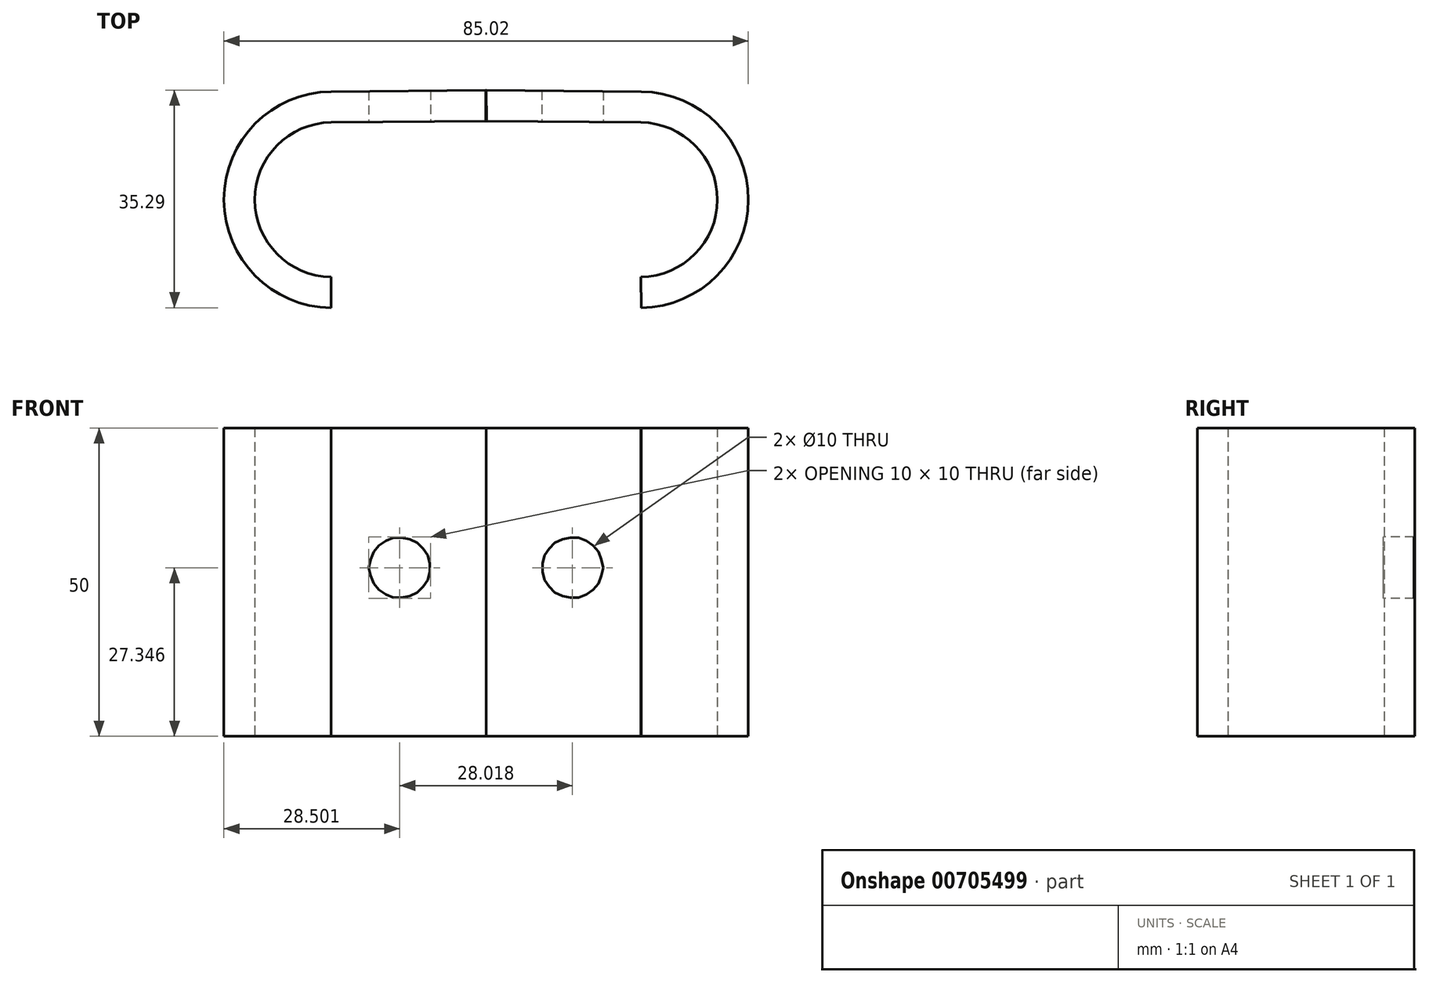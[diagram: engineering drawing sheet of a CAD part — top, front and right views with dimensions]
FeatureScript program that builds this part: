
annotation { "Feature Type Name" : "Feature", "Feature Type Description" : "" }
export const myFeature = defineFeature(function(context is Context, id is Id, definition is map)
    precondition{}
    {
        {
            var Q0;
            Q0=qCreatedBy(makeId("Top.planeOp"),FACE);
            var sketch = newSketch(context, id + "F0", { "sketchPlane" : qUnion([Q0])});
            skArc(sketch, "E0", {"start": v(25.1, -15.14) * mm, "mid": v(37.51, -2.6) * mm, "end": v(25.1, 9.92) * mm});
            skLineSegment(sketch, "E1", {"start": v(25.1, 9.92) * mm, "end": v(-0.08, 10.16) * mm});
            skLineSegment(sketch, "E2.0", {"start": v(25.15, 14.92) * mm, "end": v(-0.03, 15.16) * mm});
            skArc(sketch, "E2.1", {"start": v(25.15, -20.14) * mm, "mid": v(42.51, -2.6) * mm, "end": v(25.15, 14.92) * mm});
            skLineSegment(sketch, "E3", {"start": v(25.1, -15.14) * mm, "end": v(25.15, -20.14) * mm});
            skLineSegment(sketch, "E4", {"start": v(-0.08, 10.16) * mm, "end": v(-0.03, 15.16) * mm});
            skLineSegment(sketch, "E5.MirrorCS", {"start": v(0.08, 10.16) * mm, "end": v(0.03, 15.16) * mm});
            skLineSegment(sketch, "E6.MirrorCS", {"start": v(-25.1, -15.14) * mm, "end": v(-25.15, -20.14) * mm});
            skArc(sketch, "E7.MirrorCS", {"start": v(-25.15, -20.14) * mm, "mid": v(-42.51, -2.6) * mm, "end": v(-25.15, 14.92) * mm});
            skLineSegment(sketch, "E8.MirrorCS", {"start": v(-25.1, 9.92) * mm, "end": v(0.08, 10.16) * mm});
            skArc(sketch, "E9.MirrorCS", {"start": v(-25.1, -15.14) * mm, "mid": v(-37.51, -2.6) * mm, "end": v(-25.1, 9.92) * mm});
            skLineSegment(sketch, "E10.MirrorCS", {"start": v(-25.15, 14.92) * mm, "end": v(0.03, 15.16) * mm});
            skSolve(sketch);
        }
        {
            var Q0;
            {var subQ5=sQuery(id+"F0.wireOp",EDGE,"E0");Q0=makeQuery(id+"F0.imprint","IMPRINT",FACE,{"disambiguationData":[TD([[makeQuery(id+"F0.imprint","IMPRINT",EDGE,{"derivedFrom":subQ5}),-1.0]])]});}
            extrude(context, id + "F1", {"entities" : qUnion([Q0]), "depth" : 50 * mm, "offsetDistance" : 25 * mm});
        }
        {
            var Q0;
            Q0=makeQuery(id+"F1.opExtrude","SWEPT_BODY",BODY,{"disambiguationData":[OSD([sQuery(id+"F0.wireOp",EDGE,"E0"),sQuery(id+"F0.wireOp",EDGE,"E1"),sQuery(id+"F0.wireOp",EDGE,"E2.0"),sQuery(id+"F0.wireOp",EDGE,"E2.1"),sQuery(id+"F0.wireOp",EDGE,"E3"),sQuery(id+"F0.wireOp",EDGE,"E5.MirrorCS"),sQuery(id+"F0.wireOp",EDGE,"E8.MirrorCS")])]});
            var Q1;
            Q1=qCreatedBy(makeId("Right.planeOp"),FACE);
            mirror(context, id + "F2", {"entities" : qUnion([Q0]), "mirrorPlane" : qUnion([Q1])});
        }
        {
            var Q0;
            Q0=qCreatedBy(makeId("Front.planeOp"),FACE);
            var sketch = newSketch(context, id + "F3", { "sketchPlane" : qUnion([Q0])});
            skCircle(sketch, "E11", {"center": v(-14, 27.35) * mm, "radius": 7.5 * mm});
            skCircle(sketch, "E12.MirrorC", {"center": v(14, 27.35) * mm, "radius": 7.5 * mm});
            skSolve(sketch);
        }
        {
            var Q0;
            Q0=sQuery(id+"F3.wireOp",VERTEX,"E11.center");
            var Q1;
            Q1=sQuery(id+"F3.wireOp",VERTEX,"E12.MirrorC.center");
            var Q2;
            Q2=makeQuery(id+"F1.opExtrude","SWEPT_BODY",BODY,{"disambiguationData":[OSD([sQuery(id+"F0.wireOp",EDGE,"E0"),sQuery(id+"F0.wireOp",EDGE,"E1"),sQuery(id+"F0.wireOp",EDGE,"E2.0"),sQuery(id+"F0.wireOp",EDGE,"E2.1"),sQuery(id+"F0.wireOp",EDGE,"E3"),sQuery(id+"F0.wireOp",EDGE,"E5.MirrorCS"),sQuery(id+"F0.wireOp",EDGE,"E8.MirrorCS")])]});
            var Q3;
            Q3=makeQuery(id+"F2.opPattern","COPY",BODY,{"derivedFrom":makeQuery(id+"F1.opExtrude","SWEPT_BODY",BODY,{"disambiguationData":[OSD([sQuery(id+"F0.wireOp",EDGE,"E0"),sQuery(id+"F0.wireOp",EDGE,"E1"),sQuery(id+"F0.wireOp",EDGE,"E2.0"),sQuery(id+"F0.wireOp",EDGE,"E2.1"),sQuery(id+"F0.wireOp",EDGE,"E3"),sQuery(id+"F0.wireOp",EDGE,"E5.MirrorCS"),sQuery(id+"F0.wireOp",EDGE,"E8.MirrorCS")])]}),"instanceName":"1"});
            hole(context, id + "F4", {"style" : HoleStyle.SIMPLE, "endStyle" : HoleEndStyle.THROUGH, "holeDiameter" : 10 * mm, "majorDiameter" : 5 * mm, "isTappedThrough" : true, "tappedDepth" : 12 * mm, "tapClearance" : 3, "locations" : qUnion([Q0, Q1]), "scope" : qUnion([Q2, Q3])});
        }
    });
